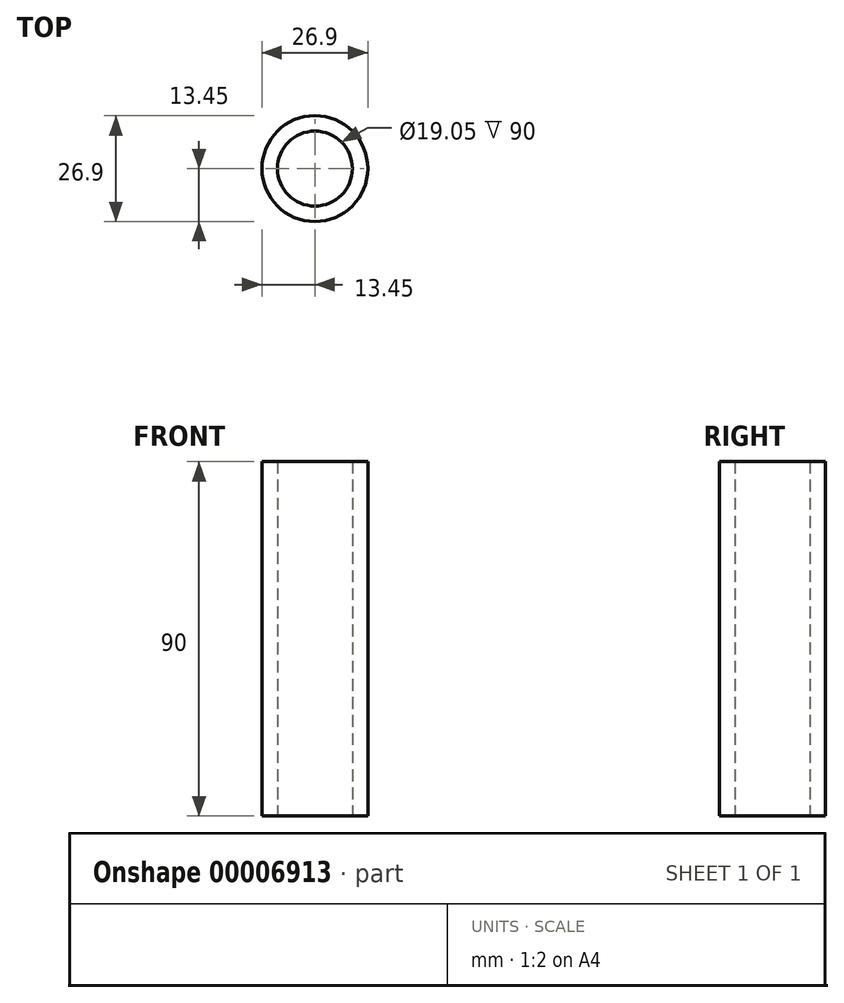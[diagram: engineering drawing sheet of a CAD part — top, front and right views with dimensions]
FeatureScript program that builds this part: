
annotation { "Feature Type Name" : "Feature", "Feature Type Description" : "" }
export const myFeature = defineFeature(function(context is Context, id is Id, definition is map)
    precondition{}
    {
        {
            var Q0;
            Q0=qCreatedBy(makeId("Top.planeOp"),FACE);
            var sketch = newSketch(context, id + "F0", { "sketchPlane" : qUnion([Q0])});
            skCircle(sketch, "E0", {"center": v(0, 0) * mm, "radius": 13.45 * mm});
            skCircle(sketch, "E1", {"center": v(0, 0) * mm, "radius": 9.53 * mm});
            skSolve(sketch);
        }
        {
            var Q0;
            Q0=makeQuery(id+"F0.imprint","IMPRINT",FACE,{"disambiguationData":[TD([[makeQuery(id+"F0.imprint","IMPRINT",EDGE,{"derivedFrom":sQuery(id+"F0.wireOp",EDGE,"E0")}),1.0]])]});
            extrude(context, id + "F1", {"entities" : qUnion([Q0]), "depth" : 90 * mm});
        }
    });
